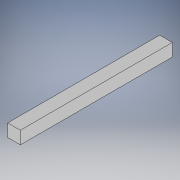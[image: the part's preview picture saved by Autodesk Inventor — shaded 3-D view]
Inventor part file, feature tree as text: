
AUTODESK INVENTOR PART (.ipt)
format: ipt  version: 2018 (Build 220112000, 112)  size: 91,136 bytes
history: native  units: in
note: dims shown in document units (in); Inventor stores cm internally (conversion verified against a paired STEP export)
features: extrude x1, sketch x1
ambient origin geometry x8: Origin, YZ Plane, XZ Plane, XY Plane, X Axis, Y Axis, Z Axis, Center Point
bodies: Solid1 (feature_tree)
feature tree (2):
  extrude  "Extrusion1"  Depth=12.0in
  sketch  "Sketch1"  dims[d0=1.0in d1=12.0in d2=1.0in d3=0.0in]
